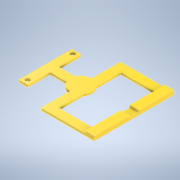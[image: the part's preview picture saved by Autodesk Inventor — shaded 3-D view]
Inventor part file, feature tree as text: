
AUTODESK INVENTOR PART (.ipt)
format: ipt  version: 2021 (Build 250183000, 183)  size: 171,520 bytes
history: native  units: mm
features: extrude x2, sketch x2, other x1, projected_geometry x1
ambient origin geometry x8: Origin, YZ Plane, XZ Plane, XY Plane, X Axis, Y Axis, Z Axis, Center Point
bodies: Solid1 (feature_tree)
feature tree (6):
  other  "<userpath>\Documents\Semestre8\Robótica\Proyecto-Rob\Piezas\ParámetrosGripper.xlsx"
  extrude  "Extrusion1"  Depth=20.0mm
  extrude  "Extrusion2"  Depth=200.0mm
  sketch  "Sketch1"  dims[d0=20.0mm d1=20.0mm]
  sketch  "Sketch2"  dims[d2=20.0mm d3=200.0mm d4=120.0mm d5=120.0mm d6=180.0mm d7=50.0mm d8=10.0mm d9=9.0mm d10=10.0mm d11=9.0mm d12=10.0mm d13=10.0mm d14=5.0mm d15=0.0mm d16=20.0mm d17=10.0mm d18=5.0mm d19=0.0mm]
  projected_geometry  "Projected Loop1"
